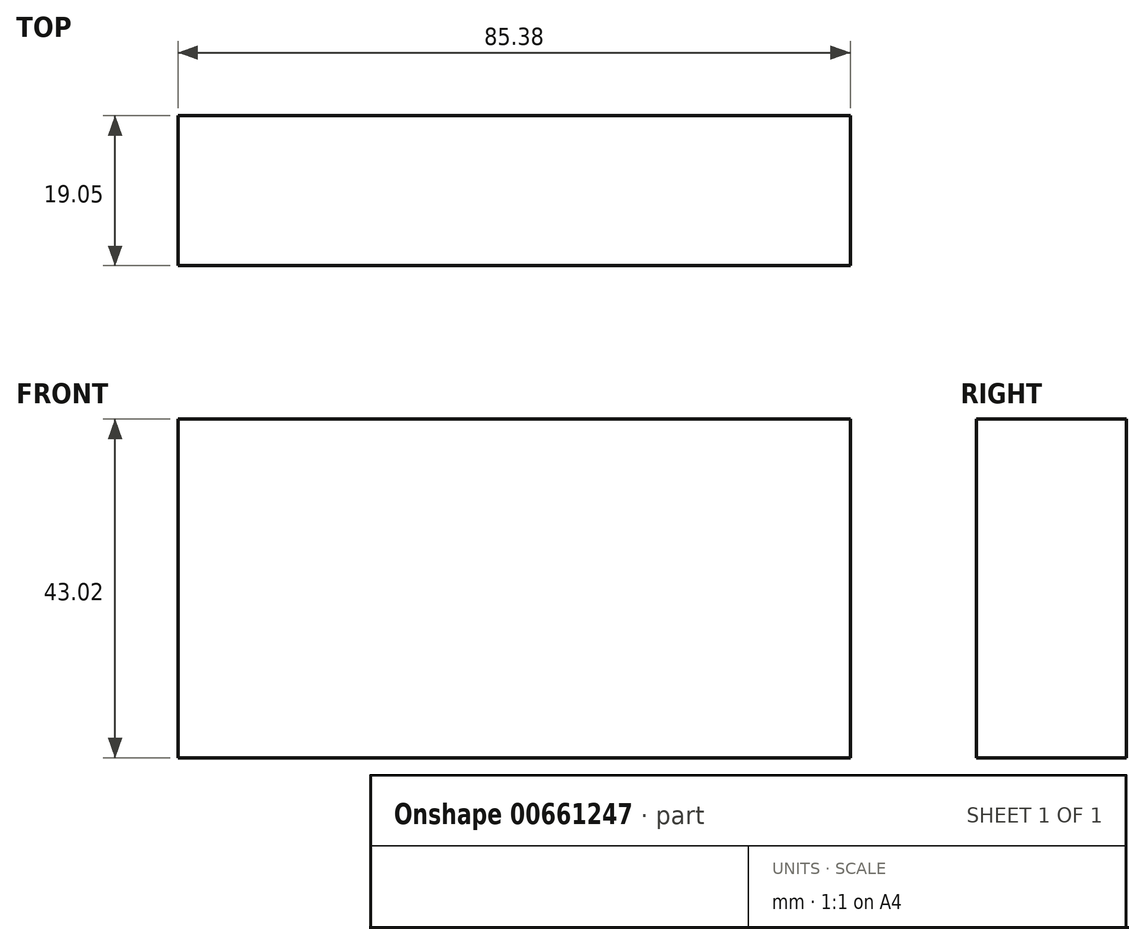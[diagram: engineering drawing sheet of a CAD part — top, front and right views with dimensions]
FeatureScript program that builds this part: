
annotation { "Feature Type Name" : "Feature", "Feature Type Description" : "" }
export const myFeature = defineFeature(function(context is Context, id is Id, definition is map)
    precondition{}
    {
        {
            var Q0;
            Q0=qCreatedBy(makeId("Front.planeOp"),FACE);
            var sketch = newSketch(context, id + "F0", { "sketchPlane" : qUnion([Q0])});
            skLineSegment(sketch, "E0.bottom", {"start": v(-43.52, 21.51) * mm, "end": v(41.86, 21.51) * mm});
            skLineSegment(sketch, "E0.top", {"start": v(-43.52, -21.51) * mm, "end": v(41.86, -21.51) * mm});
            skLineSegment(sketch, "E0.left", {"start": v(-43.52, 21.51) * mm, "end": v(-43.52, -21.51) * mm});
            skLineSegment(sketch, "E0.right", {"start": v(41.86, 21.51) * mm, "end": v(41.86, -21.51) * mm});
            skSolve(sketch);
        }
        {
            var Q0;
            Q0=makeQuery(id+"F0.imprint","IMPRINT",FACE,{"disambiguationData":[TD([[makeQuery(id+"F0.imprint","IMPRINT",EDGE,{"derivedFrom":sQuery(id+"F0.wireOp",EDGE,"E0.bottom")}),-1.0]])]});
            extrude(context, id + "F1", {"entities" : qUnion([Q0]), "depth" : 19.05 * mm, "offsetDistance" : 25.4 * mm});
        }
    });
